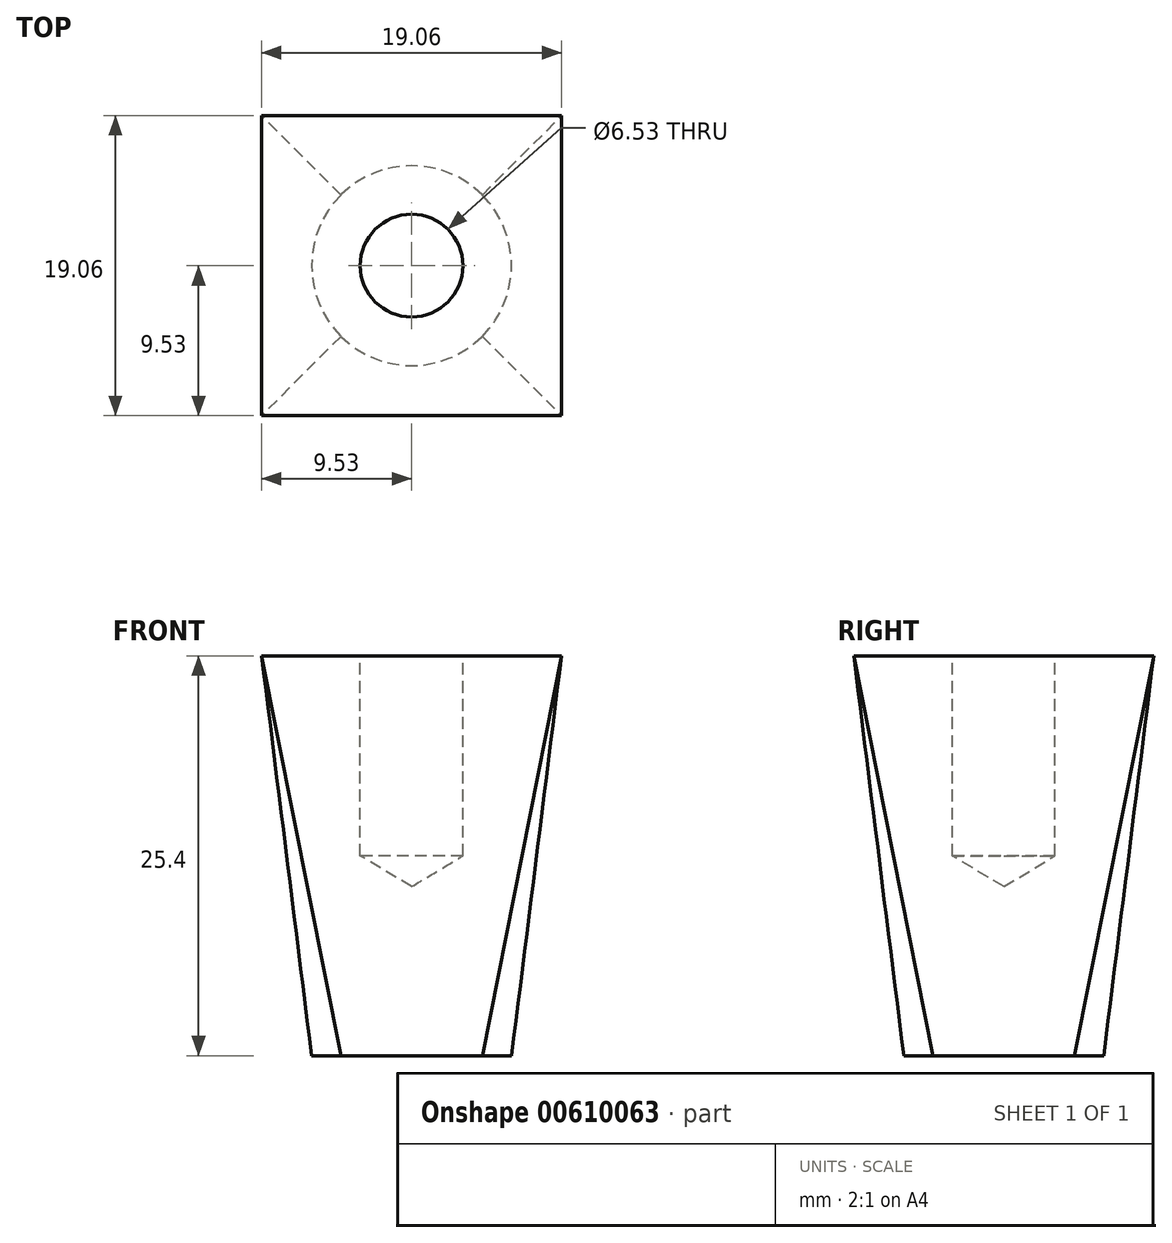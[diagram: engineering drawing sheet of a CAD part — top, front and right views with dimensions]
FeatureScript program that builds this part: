
annotation { "Feature Type Name" : "Feature", "Feature Type Description" : "" }
export const myFeature = defineFeature(function(context is Context, id is Id, definition is map)
    precondition{}
    {
        {
            var Q0;
            Q0=qCreatedBy(makeId("Top.planeOp"),FACE);
            var sketch = newSketch(context, id + "F0", { "sketchPlane" : qUnion([Q0])});
            skCircle(sketch, "E0", {"center": v(0, 0) * mm, "radius": 6.35 * mm});
            skSolve(sketch);
        }
        {
            var Q0;
            Q0=qCreatedBy(makeId("Top.planeOp"),FACE);
            cPlane(context, id + "F1", {"entities" : qUnion([Q0]), "cplaneType" : CPlaneType.OFFSET, "offset" : 25.4 * mm, "width" : 152.4 * mm, "height" : 152.4 * mm});
        }
        {
            var Q0;
            Q0=qCreatedBy(id+"F1.planeOp",FACE);
            var sketch = newSketch(context, id + "F2", { "sketchPlane" : qUnion([Q0])});
            skLineSegment(sketch, "E1.bottom", {"start": v(9.52, 9.53) * mm, "end": v(-9.53, 9.52) * mm});
            skLineSegment(sketch, "E1.top", {"start": v(9.53, -9.53) * mm, "end": v(-9.52, -9.52) * mm});
            skLineSegment(sketch, "E1.left", {"start": v(9.52, 9.53) * mm, "end": v(9.52, -9.52) * mm});
            skLineSegment(sketch, "E1.right", {"start": v(-9.53, 9.52) * mm, "end": v(-9.53, -9.53) * mm});
            skPoint(sketch, "E1.middle", {"position": v(0, 0) * mm});
            skSolve(sketch);
        }
        {
            var Q0;
            Q0=makeQuery(id+"F0.imprint","IMPRINT",FACE,{"disambiguationData":[TD([[makeQuery(id+"F0.imprint","IMPRINT",EDGE,{"derivedFrom":sQuery(id+"F0.wireOp",EDGE,"E0")}),1.0]])]});
            var Q1;
            Q1=makeQuery(id+"F2.imprint","IMPRINT",FACE,{"disambiguationData":[TD([[makeQuery(id+"F2.imprint","IMPRINT",EDGE,{"derivedFrom":sQuery(id+"F2.wireOp",EDGE,"E1.bottom")}),1.0]])]});
            loft(context, id + "F3", {"sheetProfilesArray" : [{ "sheetProfileEntities" : qUnion([Q0]) }, { "sheetProfileEntities" : qUnion([Q1]) }]});
        }
        {
            var Q0;
            Q0=makeQuery(id+"F3.opLoft","CAP_FACE",FACE,{"disambiguationData":[OSD([makeQuery(id+"F2.imprint","IMPRINT",FACE,{"disambiguationData":[TD([[makeQuery(id+"F2.imprint","IMPRINT",EDGE,{"derivedFrom":sQuery(id+"F2.wireOp",EDGE,"E1.bottom")}),1.0]])]})])],"isStart":true});
            var sketch = newSketch(context, id + "F4", { "sketchPlane" : qUnion([Q0])});
            skPoint(sketch, "E2", {"position": v(0, 0) * mm});
            skSolve(sketch);
        }
        {
            var Q0;
            Q0=sQuery(id+"F4.wireOp",VERTEX,"E2");
            var Q1;
            Q1=makeQuery(id+"F3.opLoft","SWEPT_BODY",BODY,{"disambiguationData":[OSD([makeQuery(id+"F0.imprint","IMPRINT",FACE,{"disambiguationData":[TD([[makeQuery(id+"F0.imprint","IMPRINT",EDGE,{"derivedFrom":sQuery(id+"F0.wireOp",EDGE,"E0")}),1.0]])]}),makeQuery(id+"F2.imprint","IMPRINT",FACE,{"disambiguationData":[TD([[makeQuery(id+"F2.imprint","IMPRINT",EDGE,{"derivedFrom":sQuery(id+"F2.wireOp",EDGE,"E1.bottom")}),1.0]])]})])]});
            hole(context, id + "F5", {"style" : HoleStyle.SIMPLE, "endStyle" : HoleEndStyle.BLIND, "standardTappedOrClearance" : lookupTablePath({ "standard" : "ANSI", "fit" : "Close", "size" : "1/4", "type" : "Clearance" }), "standardBlindInLast" : lookupTablePath({ "fit" : "Close", "standard" : "ANSI", "size" : "1/4", "type" : "Clearance" }), "holeDiameter" : 6.53 * mm, "majorDiameter" : 6.35 * mm, "holeDepth" : 12.7 * mm, "tappedDepth" : 12.7 * mm, "tapClearance" : 3, "startFromSketch" : true, "locations" : qUnion([Q0]), "scope" : qUnion([Q1])});
        }
    });
